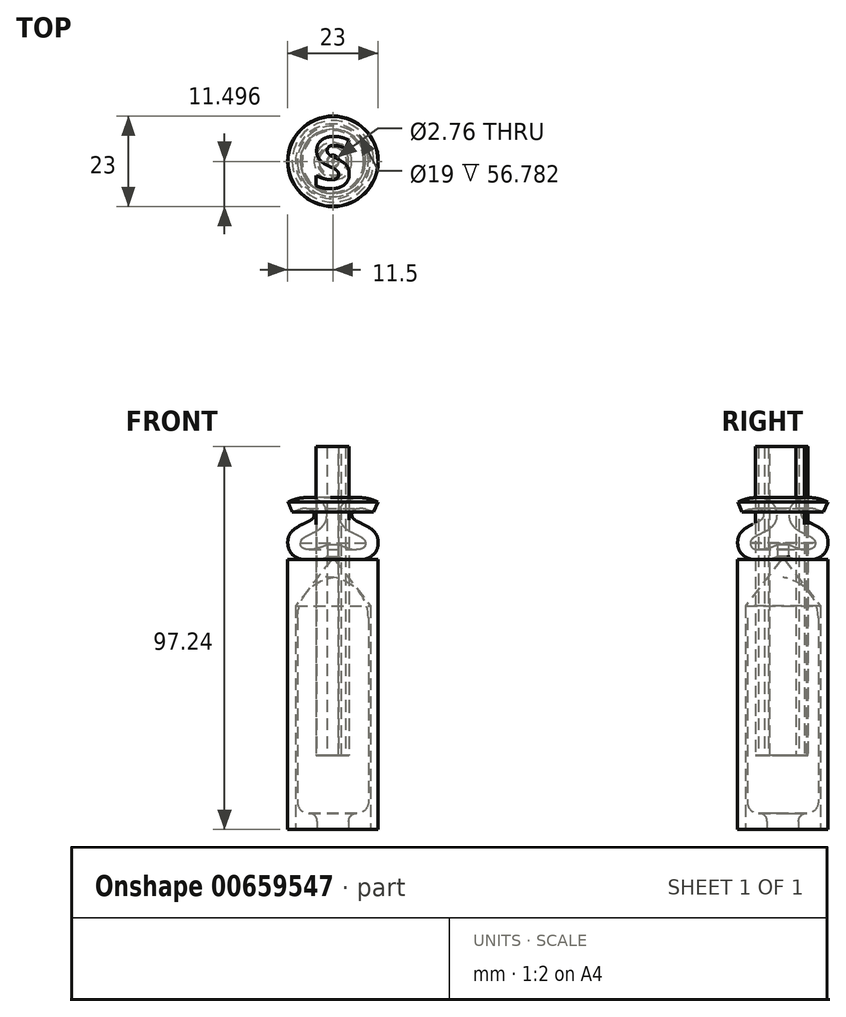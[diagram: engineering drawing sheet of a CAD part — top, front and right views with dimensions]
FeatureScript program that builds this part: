
annotation { "Feature Type Name" : "Feature", "Feature Type Description" : "" }
export const myFeature = defineFeature(function(context is Context, id is Id, definition is map)
    precondition{}
    {
        {
            var Q0;
            Q0=qCreatedBy(makeId("Right.planeOp"),FACE);
            var sketch = newSketch(context, id + "F0", { "sketchPlane" : qUnion([Q0])});
            skLineSegment(sketch, "E0", {"start": v(-4.78, -18.82) * mm, "end": v(-4.78, 45.18) * mm});
            skLineSegment(sketch, "E1", {"start": v(-4.78, -18.82) * mm, "end": v(-0.78, -18.82) * mm});
            skLineSegment(sketch, "E2", {"start": v(4.22, 34.85) * mm, "end": v(4.22, -11.89) * mm});
            skArc(sketch, "E3", {"start": v(1.32, -14.72) * mm, "mid": v(3.36, -13.92) * mm, "end": v(4.22, -11.89) * mm});
            skArc(sketch, "E4", {"start": v(1.32, -14.72) * mm, "mid": v(-0.17, -15.3) * mm, "end": v(-0.78, -16.77) * mm});
            skLineSegment(sketch, "E5", {"start": v(-0.78, -18.82) * mm, "end": v(-0.78, -16.77) * mm});
            skArc(sketch, "E6", {"start": v(4.22, 34.85) * mm, "mid": v(1.65, 41.7) * mm, "end": v(-4.78, 45.18) * mm});
            skSolve(sketch);
        }
        {
            var Q0;
            Q0 = qSketchRegion(id + "F0", true);
            var Q1;
            Q1=sQuery(id+"F0.wireOp",EDGE,"E0");
            revolve(context, id + "F1", {"entities" : qUnion([Q0]), "axis" : qUnion([Q1]), "revolveType" : RevolveType.FULL});
        }
        {
            var Q0;
            Q0=qCreatedBy(makeId("Right.planeOp"),FACE);
            var sketch = newSketch(context, id + "F2", { "sketchPlane" : qUnion([Q0])});
            skLineSegment(sketch, "E7", {"start": v(4.72, 37.94) * mm, "end": v(4.72, -18.84) * mm});
            skLineSegment(sketch, "E8", {"start": v(4.72, -18.84) * mm, "end": v(6.72, -18.84) * mm});
            skLineSegment(sketch, "E9", {"start": v(6.72, -18.84) * mm, "end": v(6.72, 49.74) * mm});
            skLineSegment(sketch, "E10", {"start": v(6.72, 49.74) * mm, "end": v(-4.4, 49.74) * mm});
            skLineSegment(sketch, "E11", {"start": v(-4.4, 49.74) * mm, "end": v(4.72, 37.94) * mm});
            skText(sketch, "E12", { "text": "S", "fontName": "OpenSans-Bold.ttf"});
            skLineSegment(sketch, "E13", {"start": v(-4.4, 49.74) * mm, "end": v(-4.4, -19.06) * mm});
            const initialGuessF2  = {"E12": [-0.0044, 0.04974, 1, 0, 0.01563]};
            skSetInitialGuess(sketch, initialGuessF2);
            skSolve(sketch);
        }
        {
            var Q0;
            Q0 = qSketchRegion(id + "F2", true);
            var Q1;
            Q1=sQuery(id+"F0.wireOp",EDGE,"E0");
            revolve(context, id + "F3", {"entities" : qUnion([Q0]), "axis" : qUnion([Q1]), "revolveType" : RevolveType.FULL});
        }
        {
            var Q0;
            Q0=qCreatedBy(makeId("Top.planeOp"),FACE);
            var sketch = newSketch(context, id + "F4", { "sketchPlane" : qUnion([Q0])});
            skText(sketch, "E14", { "text": "S", "fontName": "OpenSans-Bold.ttf"});
            const initialGuessF4  = {"E14": [-0.00512, -0.01156, 1, 0, 0.01304]};
            skSetInitialGuess(sketch, initialGuessF4);
            skSolve(sketch);
        }
        {
            var Q0;
            Q0 = qSketchRegion(id + "F4", true);
            extrude(context, id + "F5", {"entities" : qUnion([Q0]), "depth" : 78.4 * mm, "offsetDistance" : 25 * mm});
        }
    });
